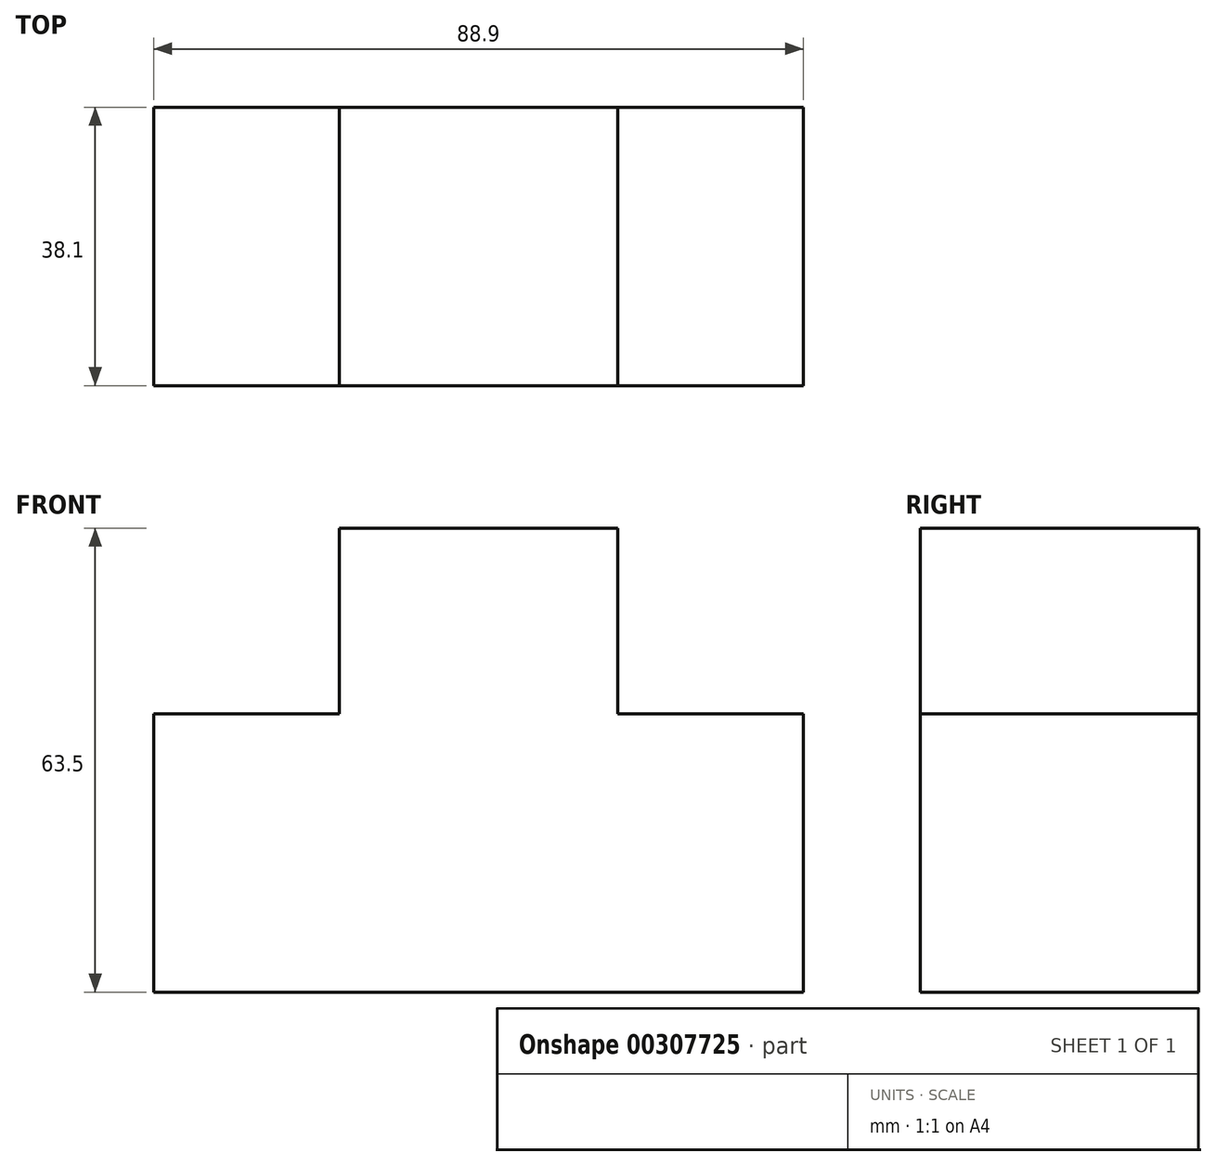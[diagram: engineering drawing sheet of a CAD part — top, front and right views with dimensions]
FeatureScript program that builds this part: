
annotation { "Feature Type Name" : "Feature", "Feature Type Description" : "" }
export const myFeature = defineFeature(function(context is Context, id is Id, definition is map)
    precondition{}
    {
        {
            var Q0;
            Q0=qCreatedBy(makeId("Front.planeOp"),FACE);
            var sketch = newSketch(context, id + "F0", { "sketchPlane" : qUnion([Q0])});
            skLineSegment(sketch, "E0", {"start": v(-37.18, -24.69) * mm, "end": v(51.72, -24.69) * mm});
            skLineSegment(sketch, "E1", {"start": v(51.72, -24.69) * mm, "end": v(51.72, 13.41) * mm});
            skLineSegment(sketch, "E2", {"start": v(51.72, 13.41) * mm, "end": v(26.32, 13.41) * mm});
            skLineSegment(sketch, "E3", {"start": v(26.32, 13.41) * mm, "end": v(26.32, 38.81) * mm});
            skLineSegment(sketch, "E4", {"start": v(26.32, 38.81) * mm, "end": v(-11.78, 38.81) * mm});
            skLineSegment(sketch, "E5", {"start": v(-11.78, 38.81) * mm, "end": v(-11.78, 13.41) * mm});
            skLineSegment(sketch, "E6", {"start": v(-11.78, 13.41) * mm, "end": v(-37.18, 13.41) * mm});
            skLineSegment(sketch, "E7", {"start": v(-37.18, 13.41) * mm, "end": v(-37.18, -24.69) * mm});
            skSolve(sketch);
        }
        {
            var Q0;
            Q0=makeQuery(id+"F0.imprint","IMPRINT",FACE,{"disambiguationData":[TD([[makeQuery(id+"F0.imprint","IMPRINT",EDGE,{"derivedFrom":sQuery(id+"F0.wireOp",EDGE,"E0")}),1.0]])]});
            extrude(context, id + "F1", {"entities" : qUnion([Q0]), "depth" : 38.1 * mm});
        }
    });
